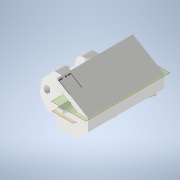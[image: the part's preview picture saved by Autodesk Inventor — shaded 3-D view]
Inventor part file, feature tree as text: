
AUTODESK INVENTOR PART (.ipt)
format: ipt  version: 2020 (Build 240168000, 168)  size: 267,264 bytes
history: native  units: mm
features: sketch x11, extrude x9, chamfer x3, reference x3, other x3, plane x2, projected_geometry x2, hole x1, fillet x1
ambient origin geometry x8: Origin, YZ Plane, XZ Plane, XY Plane, X Axis, Y Axis, Z Axis, Center Point
bodies: Volumenkörper1 (feature_tree)
feature tree (35):
  extrude  "Extrusion1"  Depth=4.0mm
  plane  "Arbeitsebene1"
  extrude  "Extrusion2"  Depth=8.0mm TaperAngle=0.0deg
  extrude  "Extrusion3"  TaperAngle=0.0deg  [1 undecoded]
  chamfer  "Fase1"  Distance=2.0mm Angle=45.0deg
  plane  "Arbeitsebene2"
  extrude  "Extrusion6"  Depth=12.0mm
  extrude  "Extrusion7"  Depth=12.0mm TaperAngle=0.0deg
  extrude  "Extrusion8"  TaperAngle=0.0deg  [1 undecoded]
  extrude  "Extrusion9"  Depth=5.0mm
  extrude  "Extrusion10"  Depth=2.0mm
  extrude  "Extrusion11"  TaperAngle=0.0deg  [1 undecoded]
  hole  "Bohrung1"  [1 undecoded]
  chamfer  "Fase2"  Distance=2.0mm Angle=45.0deg
  fillet  "Rundung1"  Radius=2.0mm
  chamfer  "Fase3"  Distance=2.0mm Angle=45.0deg
  sketch  "Skizze14"  dims[d45=2.1mm d46=6.0mm d47=4.0mm d48=2.0mm d49=90.0deg d50=8.0mm d51=20.594885mm d52=2.0mm d53=2.0mm d54=45.0deg d55=2.0mm d56=4.0mm d57=2.0mm d58=45.0deg d59=4.0mm]
  sketch  "Skizze1"  dims[d5=4.122006mm d6=4.0mm]
  reference  "Referenz1"
  reference  "Referenz2"
  sketch  "Skizze3"  dims[d7=25.0mm d8=0.0mm d11=8.0mm d12=0.0mm]
  projected_geometry  "Projizierte Kontur1"
  sketch  "Skizze4"  dims[d13=2.032mm d14=0.0mm d15=0.0mm d22=4.0mm d23=2.0mm d24=45.0deg]
  reference  "Referenz3"
  sketch  "Skizze7"  dims[d25=10.0mm d26=12.0mm]
  sketch  "Skizze8"  dims[d27=12.0mm d28=15.0mm d29=0.0mm]
  sketch  "Skizze9"  dims[d30=8.1mm d31=0.0mm d32=0.0mm]
  sketch  "Skizze10"  dims[d33=0.0mm d34=0.0mm d35=5.0mm]
  sketch  "Skizze11"  dims[d36=0.0mm d37=0.0mm d38=2.0mm]
  sketch  "Skizze12"  dims[d39=4.0mm d40=0.0mm d41=0.0mm]
  projected_geometry  "Projizierte Kontur3"
  sketch  "Skizze13"  dims[d42=15.0mm d43=0.0mm d44=2.0mm]
  parser-record x1  (decoder bookkeeping rows leaked as tree rows — omitted from the tree; the rows remain in map.json)
  other  "GlassesAssembly.iam"
  other  "CameraArm:1"
note: 4 required parameter values undecoded (feature->parameter linkage not recoverable at this tier; creation-order binding heuristic only, values carry confidence <= 0.55)
note: 1 file-system path scrubbed to <path> (originals preserved in map.json)
